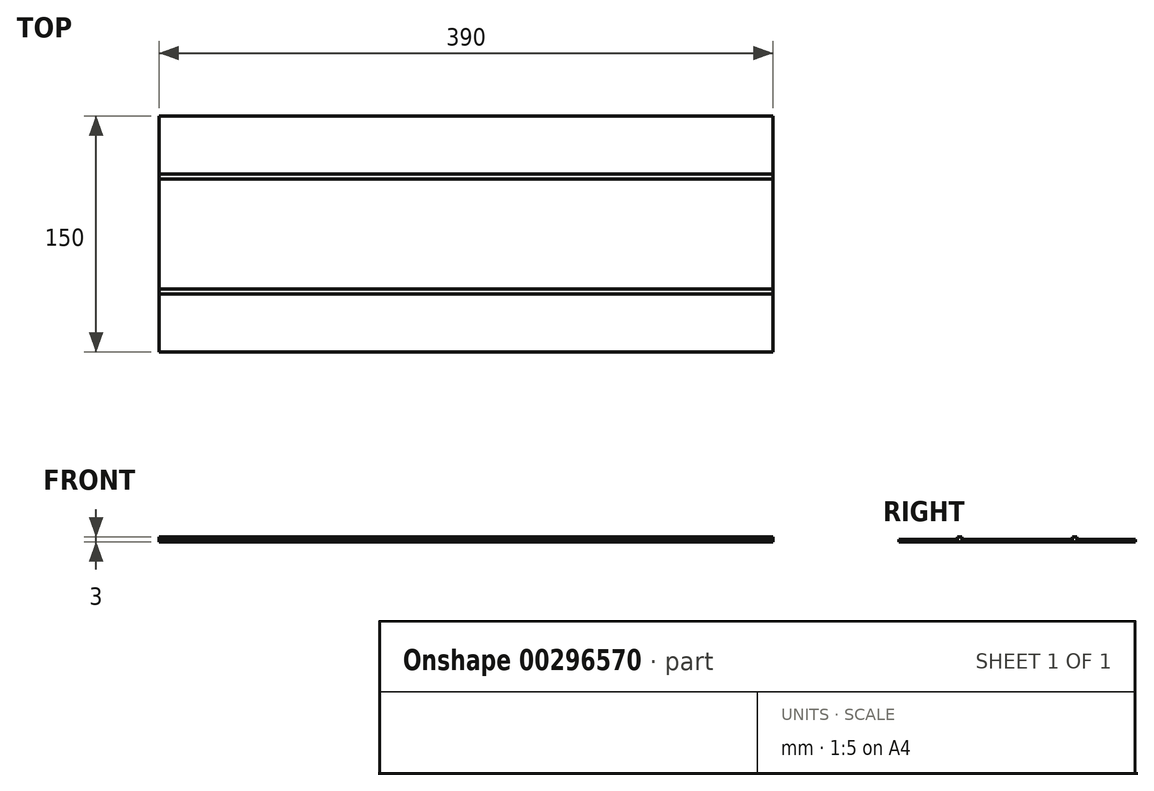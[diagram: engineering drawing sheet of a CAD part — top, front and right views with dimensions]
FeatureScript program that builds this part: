
annotation { "Feature Type Name" : "Feature", "Feature Type Description" : "" }
export const myFeature = defineFeature(function(context is Context, id is Id, definition is map)
    precondition{}
    {
        {
            var Q0;
            Q0=qCreatedBy(makeId("Top.planeOp"),FACE);
            var sketch = newSketch(context, id + "F0", { "sketchPlane" : qUnion([Q0])});
            skLineSegment(sketch, "E0.bottom", {"start": v(195, -75) * mm, "end": v(-195, -75) * mm});
            skLineSegment(sketch, "E0.top", {"start": v(195, 75) * mm, "end": v(-195, 75) * mm});
            skLineSegment(sketch, "E0.left", {"start": v(195, -75) * mm, "end": v(195, 75) * mm});
            skLineSegment(sketch, "E0.right", {"start": v(-195, -75) * mm, "end": v(-195, 75) * mm});
            skPoint(sketch, "E0.middle", {"position": v(0, 0) * mm});
            skLineSegment(sketch, "E1.bottom", {"start": v(-195, -38) * mm, "end": v(195, -38) * mm});
            skLineSegment(sketch, "E1.top", {"start": v(-195, -35) * mm, "end": v(195, -35) * mm});
            skLineSegment(sketch, "E1.left", {"start": v(-195, -38) * mm, "end": v(-195, -35) * mm});
            skLineSegment(sketch, "E1.right", {"start": v(195, -38) * mm, "end": v(195, -35) * mm});
            skLineSegment(sketch, "E2.bottom", {"start": v(-195, 35) * mm, "end": v(195, 35) * mm});
            skLineSegment(sketch, "E2.top", {"start": v(-195, 38) * mm, "end": v(195, 38) * mm});
            skLineSegment(sketch, "E2.left", {"start": v(-195, 35) * mm, "end": v(-195, 38) * mm});
            skLineSegment(sketch, "E2.right", {"start": v(195, 35) * mm, "end": v(195, 38) * mm});
            skSolve(sketch);
        }
        {
            var Q0;
            {var subQ0=sQuery(id+"F0.wireOp",EDGE,"E0.top");Q0=makeQuery(id+"F0.imprint","IMPRINT",FACE,{"disambiguationData":[TD([[makeQuery(id+"F0.imprint","IMPRINT",EDGE,{"derivedFrom":subQ0}),1.0]])]});}
            var Q1;
            {var subQ0=sQuery(id+"F0.wireOp",EDGE,"E1.top");Q1=makeQuery(id+"F0.imprint","IMPRINT",FACE,{"disambiguationData":[TD([[makeQuery(id+"F0.imprint","IMPRINT",EDGE,{"derivedFrom":subQ0}),1.0]])]});}
            var Q2;
            {var subQ0=sQuery(id+"F0.wireOp",EDGE,"E0.bottom");Q2=makeQuery(id+"F0.imprint","IMPRINT",FACE,{"disambiguationData":[TD([[makeQuery(id+"F0.imprint","IMPRINT",EDGE,{"derivedFrom":subQ0}),-1.0]])]});}
            extrude(context, id + "F1", {"entities" : qUnion([Q0, Q1, Q2]), "depth" : 1.5 * mm});
        }
        {
            var Q0;
            Q0=makeQuery(id+"F0.imprint","IMPRINT",FACE,{"disambiguationData":[TD([[makeQuery(id+"F0.imprint","IMPRINT",EDGE,{"derivedFrom":sQuery(id+"F0.wireOp",EDGE,"E2.bottom")}),1.0]])]});
            var Q1;
            Q1=makeQuery(id+"F0.imprint","IMPRINT",FACE,{"disambiguationData":[TD([[makeQuery(id+"F0.imprint","IMPRINT",EDGE,{"derivedFrom":sQuery(id+"F0.wireOp",EDGE,"E1.bottom")}),1.0]])]});
            extrude(context, id + "F2", {"entities" : qUnion([Q0, Q1]), "depth" : 3 * mm});
        }
    });
